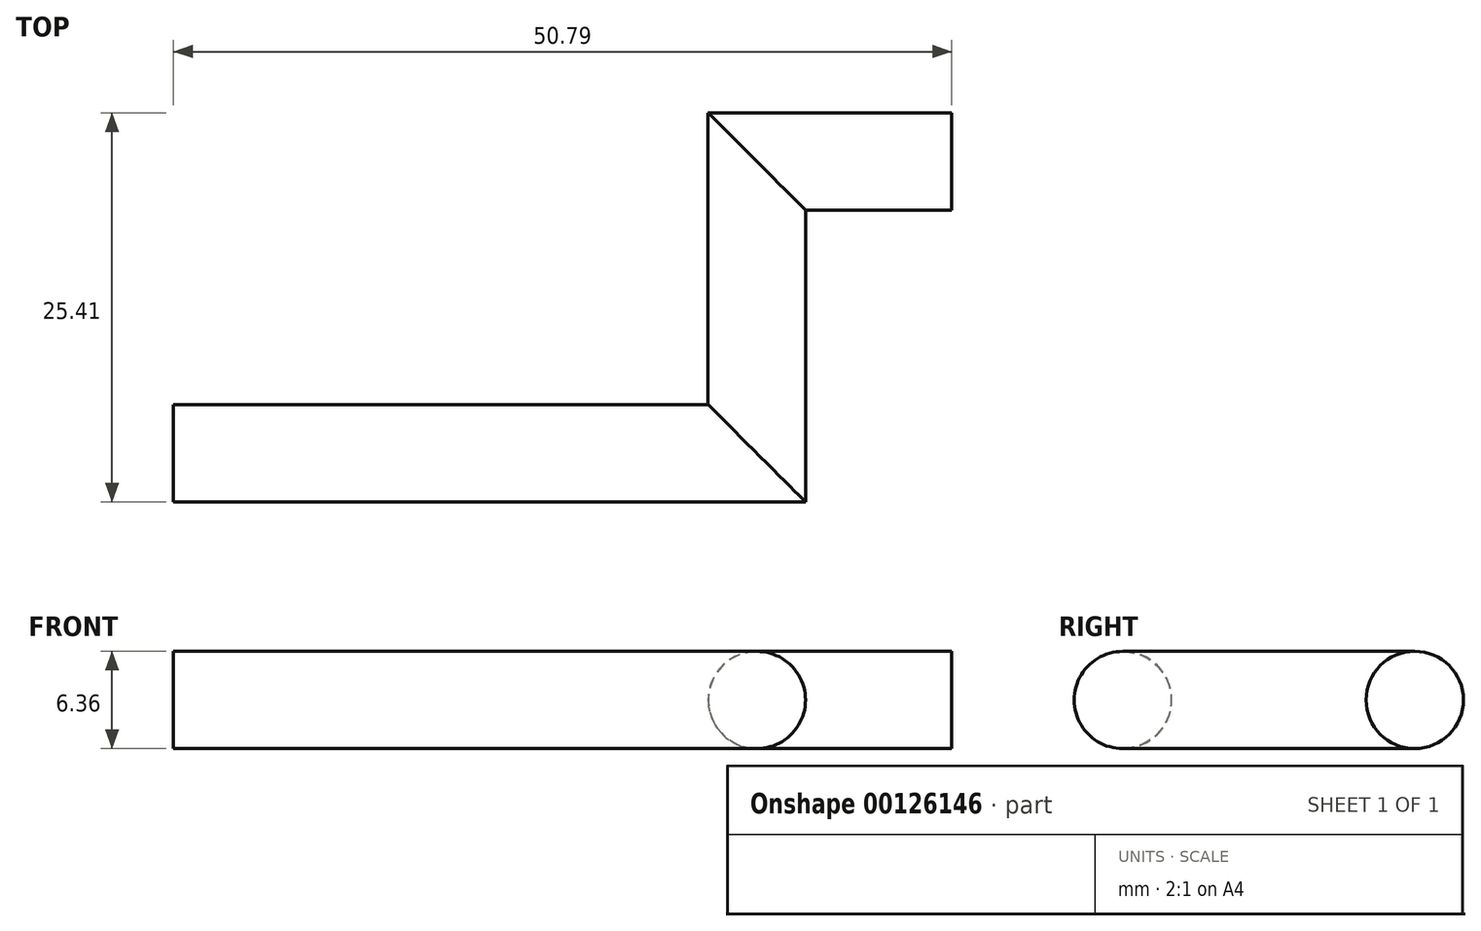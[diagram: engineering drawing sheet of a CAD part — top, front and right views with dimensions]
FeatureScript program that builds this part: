
annotation { "Feature Type Name" : "Feature", "Feature Type Description" : "" }
export const myFeature = defineFeature(function(context is Context, id is Id, definition is map)
    precondition{}
    {
        {
            var Q0;
            Q0=qCreatedBy(makeId("Top.planeOp"),FACE);
            var sketch = newSketch(context, id + "F0", { "sketchPlane" : qUnion([Q0])});
            skLineSegment(sketch, "E0", {"start": v(0, 30.44) * mm, "end": v(-12.7, 30.44) * mm});
            skLineSegment(sketch, "E1", {"start": v(-12.7, 30.44) * mm, "end": v(-12.7, 11.38) * mm});
            skLineSegment(sketch, "E2", {"start": v(-12.7, 11.38) * mm, "end": v(-50.79, 11.38) * mm});
            skSolve(sketch);
        }
        {
            var Q0;
            Q0=qCreatedBy(makeId("Right.planeOp"),FACE);
            var sketch = newSketch(context, id + "F1", { "sketchPlane" : qUnion([Q0])});
            skCircle(sketch, "E3", {"center": v(30.45, 0) * mm, "radius": 3.18 * mm});
            skSolve(sketch);
        }
        {
            var Q0;
            Q0=makeQuery(id+"F1.imprint","IMPRINT",FACE,{"disambiguationData":[TD([[makeQuery(id+"F1.imprint","IMPRINT",EDGE,{"derivedFrom":sQuery(id+"F1.wireOp",EDGE,"E3")}),1.0]])]});
            var Q1;
            Q1=sQuery(id+"F0.wireOp",EDGE,"E0");
            var Q2;
            Q2=sQuery(id+"F0.wireOp",EDGE,"E1");
            var Q3;
            Q3=sQuery(id+"F0.wireOp",EDGE,"E2");
            sweep(context, id + "F2", {"profiles" : qUnion([Q0]), "path" : qUnion([Q1, Q2, Q3])});
        }
    });
